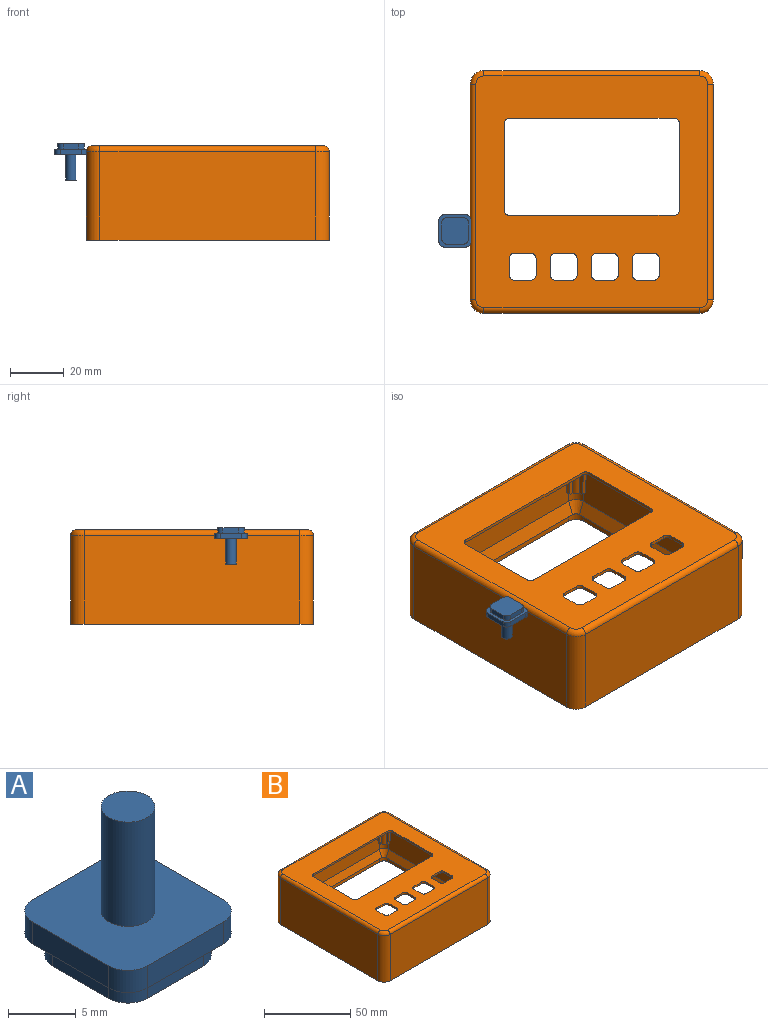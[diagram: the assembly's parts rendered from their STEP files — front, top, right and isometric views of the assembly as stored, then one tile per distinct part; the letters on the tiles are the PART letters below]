
ASSEMBLY  parts=2 mates=1
PART A: 21 faces, bbox 12x12x13.5 mm
  f0: cylinder r=2mm len=2mm, axis (0,0,-1), area 6.3mm2, adj f1,f7,f8,f9
  f1: plane 5.9x2mm, normal (0,1,0), area 11.8mm2, adj f0,f2,f8,f9
  f2: cylinder r=2mm len=2mm, axis (0,0,-1), area 6.3mm2, adj f1,f3,f8,f9
  f3: plane 5.9x2mm, normal (-1,0,0), area 11.8mm2, adj f2,f4,f8,f9
  f4: cylinder r=2mm len=2mm, axis (0,0,-1), area 6.3mm2, adj f3,f5,f8,f9
  f5: plane 5.9x2mm, normal (0,-1,0), area 11.8mm2, adj f4,f6,f8,f9
  f6: cylinder r=2mm len=2mm, axis (0,0,-1), area 6.3mm2, adj f5,f7,f8,f9
  f7: plane 5.9x2mm, normal (1,0,0), area 11.8mm2, adj f0,f6,f8,f9
  f8: plane 9.9x9.9mm, normal (0,0,-1), area 94.6mm2, adj f0,f1,f2,f3,f4,f5,f6,f7
  f9: plane 12x12mm, normal (0,0,-1), area 46mm2, adj f0,f1,f2,f3,f4,f5,f6,f7
  f10: cylinder r=2mm len=2mm, axis (0,0,-1), area 6.3mm2, adj f9,f11,f17,f18
  f11: plane 8x2mm, normal (0,1,0), area 16mm2, adj f9,f10,f12,f18
  f12: cylinder r=2mm len=2mm, axis (0,0,-1), area 6.3mm2, adj f9,f11,f13,f18
  f13: plane 8x2mm, normal (-1,0,0), area 16mm2, adj f9,f12,f14,f18
  f14: cylinder r=2mm len=2mm, axis (0,0,-1), area 6.3mm2, adj f9,f13,f15,f18
  f15: plane 8x2mm, normal (0,-1,0), area 16mm2, adj f9,f14,f16,f18
  f16: cylinder r=2mm len=2mm, axis (0,0,-1), area 6.3mm2, adj f9,f15,f17,f18
  f17: plane 8x2mm, normal (1,0,0), area 16mm2, adj f9,f10,f16,f18
  f18: plane 12x12mm, normal (0,0,1), area 128mm2, adj f10,f11,f12,f13,f14,f15,f16,f17
  f19: cylinder r=2mm len=9.46mm, axis (0,0,-1), area 118.9mm2, adj f18,f20
  f20: plane 4x4mm, normal (0,0,1), area 12.6mm2, adj f19
PART B: 168 faces, bbox 90.8x90.8x35 mm
  f0: cylinder r=3.8mm len=4mm, axis (0,0,-1), area 23.9mm2, adj f1,f7,f32,f167
  f1: plane 80x4mm, normal (0,-1,0), area 320mm2, adj f0,f2,f32,f167
  f2: cylinder r=3.8mm len=4mm, axis (0,0,-1), area 23.9mm2, adj f1,f32,f44,f167
  f3: plane 80x24mm, normal (1,0,0), area 1920mm2, adj f43,f45,f56,f162
  f4: cylinder r=3.8mm len=4mm, axis (0,0,-1), area 23.9mm2, adj f32,f44,f46,f167
  f5: plane 80x24mm, normal (0,1,0), area 1920mm2, adj f45,f47,f52,f160
  f6: cylinder r=3.8mm len=4mm, axis (0,0,-1), area 23.9mm2, adj f7,f32,f46,f167
  f7: plane 80x4mm, normal (-1,0,0), area 320mm2, adj f0,f6,f32,f167
  f8: plane 86x86mm, normal (0,0,-1), area 4501.3mm2, adj f10,f11,f12,f13,f14,f15,f16,f17
  f9: plane 86x86mm, normal (0,0,1), area 4665.4mm2, adj f33,f34,f35,f36,f37,f38,f39,f40
  f10: cylinder r=2.85mm len=14.75mm, axis (0,0,1), area 42.1mm2, adj f8,f66,f114,f118
  f11: cylinder r=2.85mm len=14.75mm, axis (0,0,1), area 42.1mm2, adj f8,f66,f110,f113
  f12: cylinder r=2.85mm len=14.75mm, axis (0,0,1), area 42.1mm2, adj f8,f66,f107,f112
  f13: cylinder r=2.85mm len=14.75mm, axis (0,0,1), area 42.1mm2, adj f8,f69,f97,f104
  f14: cylinder r=2.85mm len=14.75mm, axis (0,0,1), area 42.1mm2, adj f8,f69,f102,f106
  f15: cylinder r=2.85mm len=14.75mm, axis (0,0,1), area 42.1mm2, adj f8,f69,f98,f101
  f16: cylinder r=2.85mm len=14.75mm, axis (0,0,1), area 42.1mm2, adj f8,f69,f95,f100
  f17: cylinder r=2.85mm len=14.75mm, axis (0,0,1), area 42.1mm2, adj f8,f62,f85,f92
  f18: cylinder r=2.85mm len=14.75mm, axis (0,0,1), area 42.1mm2, adj f8,f62,f90,f94
  f19: cylinder r=2.85mm len=14.75mm, axis (0,0,1), area 42.1mm2, adj f8,f62,f86,f89
  f20: cylinder r=2.85mm len=14.75mm, axis (0,0,1), area 42.1mm2, adj f8,f62,f83,f88
  f21: cylinder r=2.85mm len=14.75mm, axis (0,0,1), area 42.1mm2, adj f8,f59,f78,f82
  f22: cylinder r=2.85mm len=14.75mm, axis (0,0,1), area 42.1mm2, adj f8,f59,f74,f77
  f23: cylinder r=2.85mm len=14.75mm, axis (0,0,1), area 42.1mm2, adj f8,f59,f71,f76
  f24: cylinder r=5mm len=33mm, axis (0,0,-1), area 259.2mm2, adj f25,f31,f32,f35
  f25: plane 80x33mm, normal (0,1,0), area 2640mm2, adj f24,f26,f32,f37
  f26: cylinder r=5mm len=33mm, axis (0,0,-1), area 259.2mm2, adj f25,f27,f32,f39
  f27: plane 80x33mm, normal (-1,0,0), area 2640mm2, adj f26,f28,f32,f40
  f28: cylinder r=5mm len=33mm, axis (0,0,-1), area 259.2mm2, adj f27,f29,f32,f38
  f29: plane 80x33mm, normal (0,-1,0), area 2640mm2, adj f28,f30,f32,f36
  f30: cylinder r=5mm len=33mm, axis (0,0,-1), area 259.2mm2, adj f29,f31,f32,f34
  f31: plane 80x33mm, normal (1,0,0), area 2640mm2, adj f24,f30,f32,f33
  f32: plane 90x90mm, normal (0,0,-1), area 417.2mm2, adj f0,f1,f2,f4,f6,f7,f24,f25
  f33: cylinder r=2mm len=80mm, axis (0,-1,0), area 251.3mm2, adj f9,f31,f34,f35
  f34: torus R=3mm, axis (0,0,1), area 21.1mm2, adj f9,f30,f33,f36
  f35: torus R=3mm, axis (0,0,1), area 21.1mm2, adj f9,f24,f33,f37
  f36: cylinder r=2mm len=80mm, axis (-1,0,0), area 251.3mm2, adj f9,f29,f34,f38
  f37: cylinder r=2mm len=80mm, axis (1,0,0), area 251.3mm2, adj f9,f25,f35,f39
  f38: torus R=3mm, axis (0,0,1), area 21.1mm2, adj f9,f28,f36,f40
  f39: torus R=3mm, axis (0,0,1), area 21.1mm2, adj f9,f26,f37,f40
  f40: cylinder r=2mm len=80mm, axis (0,1,0), area 251.3mm2, adj f9,f27,f38,f39
  f41: cylinder r=3.8mm len=24mm, axis (0,0,-1), area 143.3mm2, adj f42,f48,f51,f165
  f42: plane 80x24mm, normal (0,-1,0), area 1920mm2, adj f41,f43,f53,f164
  f43: cylinder r=3.8mm len=24mm, axis (0,0,-1), area 143.3mm2, adj f3,f42,f55,f163
  f44: plane 80x4mm, normal (1,0,0), area 320mm2, adj f2,f4,f32,f167
  f45: cylinder r=3.8mm len=24mm, axis (0,0,-1), area 143.3mm2, adj f3,f5,f54,f161
  f46: plane 80x4mm, normal (0,1,0), area 320mm2, adj f4,f6,f32,f167
  f47: cylinder r=3.8mm len=24mm, axis (0,0,-1), area 143.3mm2, adj f5,f48,f50,f159
  f48: plane 80x24mm, normal (-1,0,0), area 1920mm2, adj f41,f47,f49,f166
  f49: cylinder r=0.8mm len=80mm, axis (0,-1,0), area 100.5mm2, adj f8,f48,f50,f51
  f50: torus R=3mm, axis (0,0,1), area 6.9mm2, adj f8,f47,f49,f52
  f51: torus R=3mm, axis (0,0,1), area 6.9mm2, adj f8,f41,f49,f53
  f52: cylinder r=0.8mm len=80mm, axis (-1,0,0), area 100.5mm2, adj f5,f8,f50,f54
  f53: cylinder r=0.8mm len=80mm, axis (1,0,0), area 100.5mm2, adj f8,f42,f51,f55
  f54: torus R=3mm, axis (0,0,1), area 6.9mm2, adj f8,f45,f52,f56
  f55: torus R=3mm, axis (0,0,1), area 6.9mm2, adj f8,f43,f53,f56
  f56: cylinder r=0.8mm len=80mm, axis (0,1,0), area 100.5mm2, adj f3,f8,f54,f55
  f57: cylinder r=1.25mm len=14.75mm, axis (0,0,1), area 115.8mm2, adj f59,f60
  f58: cylinder r=2.85mm len=14.75mm, axis (0,0,1), area 42.1mm2, adj f8,f59,f73,f80
  f59: plane 7.87x7.87mm, normal (0,0,-1), area 27.8mm2, adj f21,f22,f23,f57,f58,f71,f72,f73
  f60: plane 2.5x2.5mm, normal (0,0,-1), area 4.9mm2, adj f57
  f61: cylinder r=1.25mm len=14.75mm, axis (0,0,1), area 115.8mm2, adj f62,f63
  f62: plane 7.87x7.87mm, normal (0,0,-1), area 27.8mm2, adj f17,f18,f19,f20,f61,f83,f84,f85
  f63: plane 2.5x2.5mm, normal (0,0,-1), area 4.9mm2, adj f61
  f64: cylinder r=1.25mm len=14.75mm, axis (0,0,1), area 115.8mm2, adj f66,f67
  f65: cylinder r=2.85mm len=14.75mm, axis (0,0,1), area 42.1mm2, adj f8,f66,f109,f116
  f66: plane 7.87x7.87mm, normal (0,0,-1), area 27.8mm2, adj f10,f11,f12,f64,f65,f107,f108,f109
  f67: plane 2.5x2.5mm, normal (0,0,-1), area 4.9mm2, adj f64
  f68: cylinder r=1.25mm len=14.75mm, axis (0,0,1), area 115.8mm2, adj f69,f70
  f69: plane 7.87x7.87mm, normal (0,0,-1), area 27.8mm2, adj f13,f14,f15,f16,f68,f95,f96,f97
  f70: plane 2.5x2.5mm, normal (0,0,-1), area 4.9mm2, adj f68
  f71: plane 14.75x2.5mm, normal (0,1,0), area 27.3mm2, adj f8,f23,f59,f72
  f72: plane 14.75x1.6mm, normal (1,0,-0.09), area 23.7mm2, adj f8,f59,f71,f73
  f73: plane 14.75x2.5mm, normal (0,-1,0), area 27.3mm2, adj f8,f58,f59,f72
  f74: plane 14.75x2.5mm, normal (-1,0,0), area 27.3mm2, adj f8,f22,f59,f75
  f75: plane 14.75x1.6mm, normal (0,1,-0.09), area 23.7mm2, adj f8,f59,f74,f76
  f76: plane 14.75x2.5mm, normal (1,0,0), area 27.3mm2, adj f8,f23,f59,f75
  f77: plane 14.75x2.5mm, normal (0,1,0), area 27.3mm2, adj f8,f22,f59,f79
  f78: plane 14.75x2.5mm, normal (0,-1,0), area 27.3mm2, adj f8,f21,f59,f79
  f79: plane 14.75x1.6mm, normal (-1,0,-0.09), area 23.7mm2, adj f8,f59,f77,f78
  f80: plane 14.75x2.5mm, normal (1,0,0), area 27.3mm2, adj f8,f58,f59,f81
  f81: plane 14.75x1.6mm, normal (0,-1,-0.09), area 23.7mm2, adj f8,f59,f80,f82
  f82: plane 14.75x2.5mm, normal (-1,0,0), area 27.3mm2, adj f8,f21,f59,f81
  f83: plane 14.75x2.5mm, normal (0,1,0), area 27.3mm2, adj f8,f20,f62,f84
  f84: plane 14.75x1.6mm, normal (1,0,-0.09), area 23.7mm2, adj f8,f62,f83,f85
  f85: plane 14.75x2.5mm, normal (0,-1,0), area 27.3mm2, adj f8,f17,f62,f84
  f86: plane 14.75x2.5mm, normal (-1,0,0), area 27.3mm2, adj f8,f19,f62,f87
  f87: plane 14.75x1.6mm, normal (0,1,-0.09), area 23.7mm2, adj f8,f62,f86,f88
  f88: plane 14.75x2.5mm, normal (1,0,0), area 27.3mm2, adj f8,f20,f62,f87
  f89: plane 14.75x2.5mm, normal (0,1,0), area 27.3mm2, adj f8,f19,f62,f91
  f90: plane 14.75x2.5mm, normal (0,-1,0), area 27.3mm2, adj f8,f18,f62,f91
  f91: plane 14.75x1.6mm, normal (-1,0,-0.09), area 23.7mm2, adj f8,f62,f89,f90
  f92: plane 14.75x2.5mm, normal (1,0,0), area 27.3mm2, adj f8,f17,f62,f93
  f93: plane 14.75x1.6mm, normal (0,-1,-0.09), area 23.7mm2, adj f8,f62,f92,f94
  f94: plane 14.75x2.5mm, normal (-1,0,0), area 27.3mm2, adj f8,f18,f62,f93
  f95: plane 14.75x2.5mm, normal (0,1,0), area 27.3mm2, adj f8,f16,f69,f96
  f96: plane 14.75x1.6mm, normal (1,0,-0.09), area 23.7mm2, adj f8,f69,f95,f97
  f97: plane 14.75x2.5mm, normal (0,-1,0), area 27.3mm2, adj f8,f13,f69,f96
  f98: plane 14.75x2.5mm, normal (-1,0,0), area 27.3mm2, adj f8,f15,f69,f99
  f99: plane 14.75x1.6mm, normal (0,1,-0.09), area 23.7mm2, adj f8,f69,f98,f100
  f100: plane 14.75x2.5mm, normal (1,0,0), area 27.3mm2, adj f8,f16,f69,f99
  f101: plane 14.75x2.5mm, normal (0,1,0), area 27.3mm2, adj f8,f15,f69,f103
  f102: plane 14.75x2.5mm, normal (0,-1,0), area 27.3mm2, adj f8,f14,f69,f103
  f103: plane 14.75x1.6mm, normal (-1,0,-0.09), area 23.7mm2, adj f8,f69,f101,f102
  f104: plane 14.75x2.5mm, normal (1,0,0), area 27.3mm2, adj f8,f13,f69,f105
  f105: plane 14.75x1.6mm, normal (0,-1,-0.09), area 23.7mm2, adj f8,f69,f104,f106
  f106: plane 14.75x2.5mm, normal (-1,0,0), area 27.3mm2, adj f8,f14,f69,f105
  f107: plane 14.75x2.5mm, normal (0,1,0), area 27.3mm2, adj f8,f12,f66,f108
  f108: plane 14.75x1.6mm, normal (1,0,-0.09), area 23.7mm2, adj f8,f66,f107,f109
  f109: plane 14.75x2.5mm, normal (0,-1,0), area 27.3mm2, adj f8,f65,f66,f108
  f110: plane 14.75x2.5mm, normal (-1,0,0), area 27.3mm2, adj f8,f11,f66,f111
  f111: plane 14.75x1.6mm, normal (0,1,-0.09), area 23.7mm2, adj f8,f66,f110,f112
  f112: plane 14.75x2.5mm, normal (1,0,0), area 27.3mm2, adj f8,f12,f66,f111
  f113: plane 14.75x2.5mm, normal (0,1,0), area 27.3mm2, adj f8,f11,f66,f115
  f114: plane 14.75x2.5mm, normal (0,-1,0), area 27.3mm2, adj f8,f10,f66,f115
  f115: plane 14.75x1.6mm, normal (-1,0,-0.09), area 23.7mm2, adj f8,f66,f113,f114
  f116: plane 14.75x2.5mm, normal (1,0,0), area 27.3mm2, adj f8,f65,f66,f117
  f117: plane 14.75x1.6mm, normal (0,-1,-0.09), area 23.7mm2, adj f8,f66,f116,f118
  f118: plane 14.75x2.5mm, normal (-1,0,0), area 27.3mm2, adj f8,f10,f66,f117
  f119: plane 6x1.2mm, normal (0,-1,0), area 7.2mm2, adj f8,f9,f120,f126
  f120: cylinder r=2mm len=2mm, axis (0,0,-1), area 3.8mm2, adj f8,f9,f119,f121
  f121: plane 6x1.2mm, normal (-1,0,0), area 7.2mm2, adj f8,f9,f120,f122
  f122: cylinder r=2mm len=2mm, axis (0,0,-1), area 3.8mm2, adj f8,f9,f121,f123
  f123: plane 6x1.2mm, normal (0,1,0), area 7.2mm2, adj f8,f9,f122,f124
  f124: cylinder r=2mm len=2mm, axis (0,0,-1), area 3.8mm2, adj f8,f9,f123,f125
  f125: plane 6x1.2mm, normal (1,0,0), area 7.2mm2, adj f8,f9,f124,f126
  f126: cylinder r=2mm len=2mm, axis (0,0,-1), area 3.8mm2, adj f8,f9,f119,f125
  f127: plane 6x1.2mm, normal (0,-1,0), area 7.2mm2, adj f8,f9,f128,f134
  f128: cylinder r=2mm len=2mm, axis (0,0,-1), area 3.8mm2, adj f8,f9,f127,f129
  f129: plane 6x1.2mm, normal (-1,0,0), area 7.2mm2, adj f8,f9,f128,f130
  f130: cylinder r=2mm len=2mm, axis (0,0,-1), area 3.8mm2, adj f8,f9,f129,f131
  f131: plane 6x1.2mm, normal (0,1,0), area 7.2mm2, adj f8,f9,f130,f132
  f132: cylinder r=2mm len=2mm, axis (0,0,-1), area 3.8mm2, adj f8,f9,f131,f133
  f133: plane 6x1.2mm, normal (1,0,0), area 7.2mm2, adj f8,f9,f132,f134
  f134: cylinder r=2mm len=2mm, axis (0,0,-1), area 3.8mm2, adj f8,f9,f127,f133
  f135: plane 6x1.2mm, normal (0,-1,0), area 7.2mm2, adj f8,f9,f136,f142
  f136: cylinder r=2mm len=2mm, axis (0,0,-1), area 3.8mm2, adj f8,f9,f135,f137
  f137: plane 6x1.2mm, normal (-1,0,0), area 7.2mm2, adj f8,f9,f136,f138
  f138: cylinder r=2mm len=2mm, axis (0,0,-1), area 3.8mm2, adj f8,f9,f137,f139
  f139: plane 6x1.2mm, normal (0,1,0), area 7.2mm2, adj f8,f9,f138,f140
  f140: cylinder r=2mm len=2mm, axis (0,0,-1), area 3.8mm2, adj f8,f9,f139,f141
  f141: plane 6x1.2mm, normal (1,0,0), area 7.2mm2, adj f8,f9,f140,f142
  f142: cylinder r=2mm len=2mm, axis (0,0,-1), area 3.8mm2, adj f8,f9,f135,f141
  f143: cylinder r=2mm len=2mm, axis (0,0,-1), area 3.8mm2, adj f8,f9,f144,f150
  f144: plane 6x1.2mm, normal (0,1,0), area 7.2mm2, adj f8,f9,f143,f145
  f145: cylinder r=2mm len=2mm, axis (0,0,-1), area 3.8mm2, adj f8,f9,f144,f146
  f146: plane 6x1.2mm, normal (1,0,0), area 7.2mm2, adj f8,f9,f145,f147
  f147: cylinder r=2mm len=2mm, axis (0,0,-1), area 3.8mm2, adj f8,f9,f146,f148
  f148: plane 6x1.2mm, normal (0,-1,0), area 7.2mm2, adj f8,f9,f147,f149
  f149: cylinder r=2mm len=2mm, axis (0,0,-1), area 3.8mm2, adj f8,f9,f148,f150
  f150: plane 6x1.2mm, normal (-1,0,0), area 7.2mm2, adj f8,f9,f143,f149
  f151: cylinder r=2mm len=2mm, axis (0,0,-1), area 3.8mm2, adj f8,f9,f152,f158
  f152: plane 61x1.2mm, normal (0,1,0), area 73.2mm2, adj f8,f9,f151,f153
  f153: cylinder r=2mm len=2mm, axis (0,0,-1), area 3.8mm2, adj f8,f9,f152,f154
  f154: plane 32x1.2mm, normal (1,0,0), area 38.4mm2, adj f8,f9,f153,f155
  f155: cylinder r=2mm len=2mm, axis (0,0,-1), area 3.8mm2, adj f8,f9,f154,f156
  f156: plane 61x1.2mm, normal (0,-1,0), area 73.2mm2, adj f8,f9,f155,f157
  f157: cylinder r=2mm len=2mm, axis (0,0,-1), area 3.8mm2, adj f8,f9,f156,f158
  f158: plane 32x1.2mm, normal (-1,0,0), area 38.4mm2, adj f8,f9,f151,f157
  f159: cone r=1.8mm half-angle=21.8deg, axis (0,0,1), area 23.7mm2, adj f47,f160,f166,f167
  f160: plane 80x5mm, normal (0,0.93,0.37), area 430.8mm2, adj f5,f159,f161,f167
  f161: cone r=1.8mm half-angle=21.8deg, axis (0,0,1), area 23.7mm2, adj f45,f160,f162,f167
  f162: plane 80x5mm, normal (0.93,0,0.37), area 430.8mm2, adj f3,f161,f163,f167
  f163: cone r=1.8mm half-angle=21.8deg, axis (0,0,1), area 23.7mm2, adj f43,f162,f164,f167
  f164: plane 80x5mm, normal (0,-0.93,0.37), area 430.8mm2, adj f42,f163,f165,f167
  f165: cone r=1.8mm half-angle=21.8deg, axis (0,0,1), area 23.7mm2, adj f41,f164,f166,f167
  f166: plane 80x5mm, normal (-0.93,0,0.37), area 430.8mm2, adj f48,f159,f165,f167
  f167: plane 87.6x87.6mm, normal (0,0,-1), area 675.2mm2, adj f0,f1,f2,f4,f6,f7,f44,f46
PLACE A rot(axis=(0,-1,0),180deg) t=(-156.65,-12.12,-34.74)mm
PLACE B t=(-105.94,2.32,-70.54)mm
MATE planar B.f8 <-> A.f19  axis (0,0,-1) through (-105.69,-0.12,-36.74)mm
